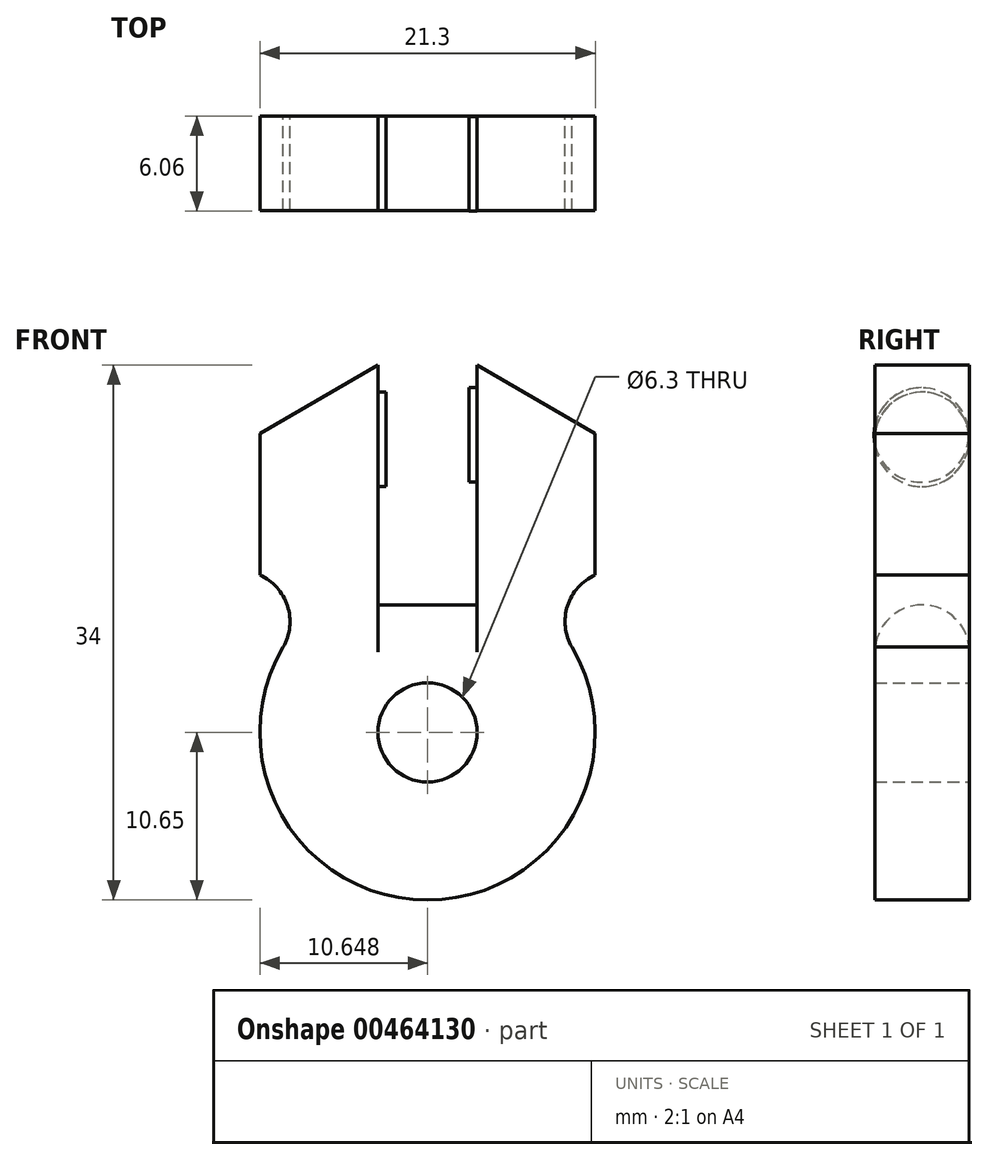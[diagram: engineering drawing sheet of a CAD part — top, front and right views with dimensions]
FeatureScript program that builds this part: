
annotation { "Feature Type Name" : "Feature", "Feature Type Description" : "" }
export const myFeature = defineFeature(function(context is Context, id is Id, definition is map)
    precondition{}
    {
        {
            var Q0;
            Q0=qCreatedBy(makeId("Front.planeOp"),FACE);
            var sketch = newSketch(context, id + "F0", { "sketchPlane" : qUnion([Q0])});
            skArc(sketch, "E0", {"start": v(-38.91, 42.77) * mm, "mid": v(-35.76, 21.95) * mm, "end": v(-32.61, 42.77) * mm});
            skCircle(sketch, "E1", {"center": v(-35.76, 32.6) * mm, "radius": 3.15 * mm});
            skLineSegment(sketch, "E2", {"start": v(-35.76, 32.6) * mm, "end": v(-35.76, 35.75) * mm});
            skLineSegment(sketch, "E3", {"start": v(-35.76, 40.7) * mm, "end": v(-32.61, 40.7) * mm});
            skLineSegment(sketch, "E4", {"start": v(-35.76, 40.7) * mm, "end": v(-38.91, 40.7) * mm});
            skLineSegment(sketch, "E5", {"start": v(-38.91, 40.7) * mm, "end": v(-38.91, 55.95) * mm});
            skLineSegment(sketch, "E6", {"start": v(-32.61, 40.7) * mm, "end": v(-32.61, 55.95) * mm});
            skLineSegment(sketch, "E7", {"start": v(-46.41, 51.6) * mm, "end": v(-38.91, 55.95) * mm});
            skLineSegment(sketch, "E8", {"start": v(-46.41, 51.6) * mm, "end": v(-46.41, 42.6) * mm});
            skLineSegment(sketch, "E9", {"start": v(-35.76, 32.6) * mm, "end": v(-38.91, 32.6) * mm});
            skArc(sketch, "E10", {"start": v(-44.93, 38.02) * mm, "mid": v(-44.65, 40.64) * mm, "end": v(-46.41, 42.6) * mm});
            skArc(sketch, "E11.MirrorCS", {"start": v(-26.6, 38.02) * mm, "mid": v(-26.87, 40.64) * mm, "end": v(-25.11, 42.6) * mm});
            skLineSegment(sketch, "E12.MirrorCS", {"start": v(-25.11, 51.6) * mm, "end": v(-25.11, 42.6) * mm});
            skLineSegment(sketch, "E13.MirrorCS", {"start": v(-25.11, 51.6) * mm, "end": v(-32.61, 55.95) * mm});
            skSolve(sketch);
        }
        {
            var Q0;
            Q0=qSketchRegion(id+"F0",true);
            extrude(context, id + "F1", {"entities" : qUnion([Q0]), "depth" : 6 * mm});
        }
        {
            var Q0;
            Q0=makeQuery(id+"F1.opExtrude","SWEPT_FACE",FACE,{"disambiguationData":[OSD([sQuery(id+"F0.wireOp",EDGE,"E6")])]});
            var sketch = newSketch(context, id + "F2", { "sketchPlane" : qUnion([Q0])});
            skLineSegment(sketch, "E14", {"start": v(3, 54.49) * mm, "end": v(3, 54.45) * mm});
            skPoint(sketch, "E14.endSnap0", {"position": v(3, 55.95) * mm});
            skCircle(sketch, "E15", {"center": v(3.06, 51.5) * mm, "radius": 3 * mm});
            skSolve(sketch);
        }
        {
            var Q0;
            Q0=qSketchRegion(id+"F2",true);
            extrude(context, id + "F3", {"entities" : qUnion([Q0]), "operationType" : NewBodyOperationType.ADD, "depth" : .5 * mm});
        }
        {
            var Q0;
            Q0=makeQuery(id+"F1.opExtrude","SWEPT_FACE",FACE,{"disambiguationData":[OSD([sQuery(id+"F0.wireOp",EDGE,"E5")])]});
            var sketch = newSketch(context, id + "F4", { "sketchPlane" : qUnion([Q0])});
            skLineSegment(sketch, "E16", {"start": v(-3, 55.95) * mm, "end": v(-3, 54.45) * mm});
            skCircle(sketch, "E17", {"center": v(-3.02, 51.21) * mm, "radius": 3 * mm});
            skSolve(sketch);
        }
        {
            var Q0;
            Q0=qSketchRegion(id+"F4",true);
            extrude(context, id + "F5", {"entities" : qUnion([Q0]), "operationType" : NewBodyOperationType.ADD, "depth" : .5 * mm});
        }
        {
            var Q0;
            Q0=qSketchRegion(id+"F0",true);
            extrude(context, id + "F6", {"entities" : qUnion([Q0]), "operationType" : NewBodyOperationType.ADD, "depth" : 6 * mm});
        }
        {
            var Q0;
            Q0=makeQuery(id+"F1.opExtrude","CAP_EDGE",EDGE,{"disambiguationData":[OSD([sQuery(id+"F0.wireOp",EDGE,"E3"),sQuery(id+"F0.wireOp",EDGE,"E4")])],"isStart":false});
            fillet(context, id + "F7", {"entities" : qUnion([Q0]), "radius" : 3 * mm, "tangentPropagation" : true, "allowEdgeOverflow" : false});
        }
        {
            var Q0;
            Q0=makeQuery(id+"F1.opExtrude","CAP_EDGE",EDGE,{"disambiguationData":[OSD([sQuery(id+"F0.wireOp",EDGE,"E3"),sQuery(id+"F0.wireOp",EDGE,"E4")])],"isStart":true});
            fillet(context, id + "F8", {"entities" : qUnion([Q0]), "radius" : 3 * mm, "tangentPropagation" : true, "allowEdgeOverflow" : false});
        }
    });
